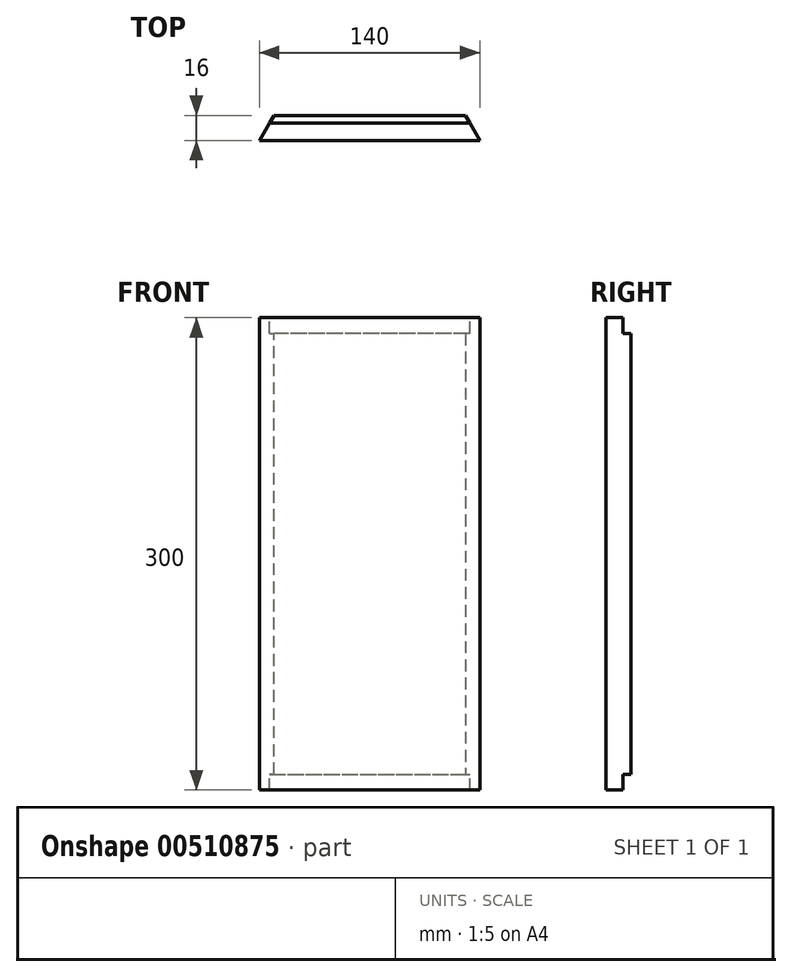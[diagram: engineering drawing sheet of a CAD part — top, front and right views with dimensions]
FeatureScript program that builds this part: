
annotation { "Feature Type Name" : "Feature", "Feature Type Description" : "" }
export const myFeature = defineFeature(function(context is Context, id is Id, definition is map)
    precondition{}
    {
        {
            var Q0;
            Q0=qCreatedBy(makeId("Front.planeOp"),FACE);
            var sketch = newSketch(context, id + "F0", { "sketchPlane" : qUnion([Q0])});
            skLineSegment(sketch, "E0.bottom", {"start": v(70, 150) * mm, "end": v(-70, 150) * mm});
            skLineSegment(sketch, "E0.top", {"start": v(70, -150) * mm, "end": v(-70, -150) * mm});
            skLineSegment(sketch, "E0.left", {"start": v(70, 150) * mm, "end": v(70, -150) * mm});
            skLineSegment(sketch, "E0.right", {"start": v(-70, 150) * mm, "end": v(-70, -150) * mm});
            skPoint(sketch, "E0.middle", {"position": v(0, 0) * mm});
            skSolve(sketch);
        }
        {
            var Q0;
            Q0=makeQuery(id+"F0.imprint","IMPRINT",FACE,{"disambiguationData":[TD([[makeQuery(id+"F0.imprint","IMPRINT",EDGE,{"derivedFrom":sQuery(id+"F0.wireOp",EDGE,"E0.bottom")}),1.0]])]});
            extrude(context, id + "F1", {"entities" : qUnion([Q0]), "depth" : 16 * mm});
        }
        {
            var Q0;
            Q0=makeQuery(id+"F1.opExtrude","CAP_EDGE",EDGE,{"disambiguationData":[OSD([sQuery(id+"F0.wireOp",EDGE,"E0.left")])],"isStart":true});
            chamfer(context, id + "F2", {"entities" : qUnion([Q0]), "chamferType" : ChamferType.OFFSET_ANGLE, "width" : 16 * mm, "oppositeDirection" : true, "angle" : 30 * degree, "tangentPropagation" : true});
        }
        {
            var Q0;
            Q0=makeQuery(id+"F1.opExtrude","CAP_EDGE",EDGE,{"disambiguationData":[OSD([sQuery(id+"F0.wireOp",EDGE,"E0.right")])],"isStart":true});
            chamfer(context, id + "F3", {"entities" : qUnion([Q0]), "chamferType" : ChamferType.OFFSET_ANGLE, "width" : 16 * mm, "oppositeDirection" : false, "angle" : 30 * degree, "tangentPropagation" : true});
        }
        {
            var Q0;
            Q0=makeQuery(id+"F1.opExtrude","CAP_FACE",FACE,{"disambiguationData":[OSD([sQuery(id+"F0.wireOp",EDGE,"E0.bottom"),sQuery(id+"F0.wireOp",EDGE,"E0.top"),sQuery(id+"F0.wireOp",EDGE,"E0.left"),sQuery(id+"F0.wireOp",EDGE,"E0.right")])],"isStart":true});
            var sketch = newSketch(context, id + "F4", { "sketchPlane" : qUnion([Q0])});
            skLineSegment(sketch, "E1.bottom", {"start": v(-100, 150) * mm, "end": v(154.39, 150) * mm});
            skLineSegment(sketch, "E1.top", {"start": v(-100, 140) * mm, "end": v(154.39, 140) * mm});
            skLineSegment(sketch, "E1.left", {"start": v(-100, 150) * mm, "end": v(-100, 140) * mm});
            skLineSegment(sketch, "E1.right", {"start": v(154.39, 150) * mm, "end": v(154.39, 140) * mm});
            skLineSegment(sketch, "E2.bottom", {"start": v(102.93, -150) * mm, "end": v(-96.66, -150) * mm});
            skLineSegment(sketch, "E2.top", {"start": v(102.93, -140) * mm, "end": v(-96.66, -140) * mm});
            skLineSegment(sketch, "E2.left", {"start": v(102.93, -150) * mm, "end": v(102.93, -140) * mm});
            skLineSegment(sketch, "E2.right", {"start": v(-96.66, -150) * mm, "end": v(-96.66, -140) * mm});
            skSolve(sketch);
        }
        {
            var Q0;
            Q0=qSketchRegion(id+"F4",true);
            extrude(context, id + "F5", {"entities" : qUnion([Q0]), "operationType" : NewBodyOperationType.REMOVE, "flatOperationType" : FlatOperationType.REMOVE, "oppositeDirection" : true, "offsetDistance" : 25 * mm, "depth" : 5 * mm, "domain" : OperationDomain.MODEL});
        }
    });
